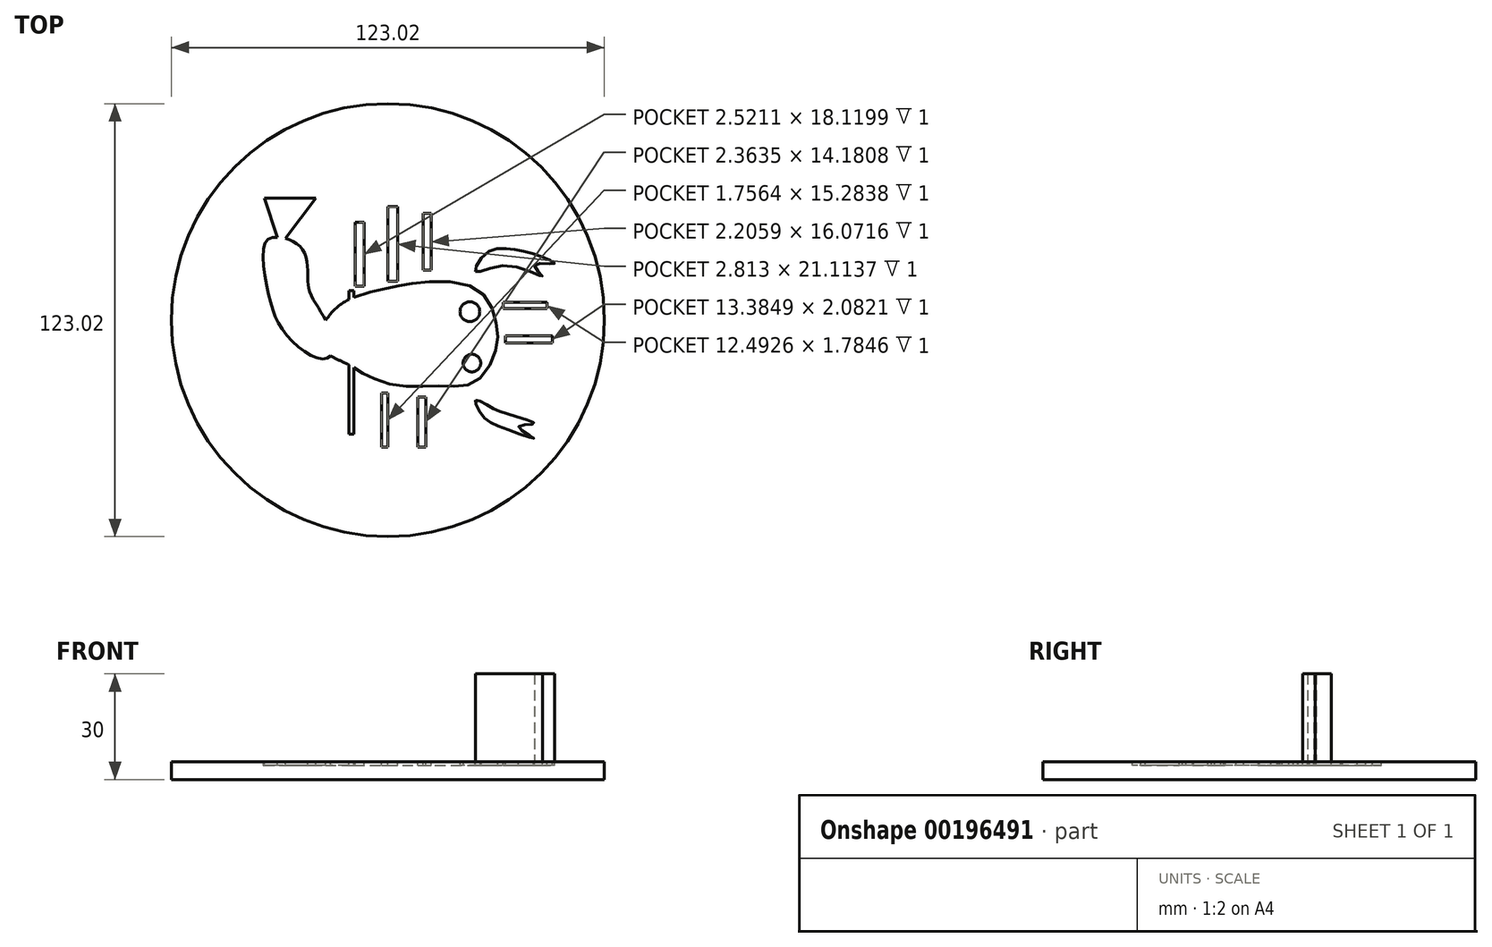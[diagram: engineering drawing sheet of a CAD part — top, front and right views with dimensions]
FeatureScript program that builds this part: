
annotation { "Feature Type Name" : "Feature", "Feature Type Description" : "" }
export const myFeature = defineFeature(function(context is Context, id is Id, definition is map)
    precondition{}
    {
        {
            var Q0;
            Q0=qCreatedBy(makeId("Top.planeOp"),FACE);
            var sketch = newSketch(context, id + "F0", { "sketchPlane" : qUnion([Q0])});
            skCircle(sketch, "E0", {"center": v(0, 0) * mm, "radius": 61.51 * mm});
            skSolve(sketch);
        }
        {
            var Q0;
            Q0=makeQuery(id+"F0.imprint","IMPRINT",FACE,{"disambiguationData":[TD([[makeQuery(id+"F0.imprint","IMPRINT",EDGE,{"derivedFrom":sQuery(id+"F0.wireOp",EDGE,"E0")}),1.0]])]});
            extrude(context, id + "F1", {"entities" : qUnion([Q0]), "depth" : 5 * mm});
        }
        {
            var Q0;
            Q0=makeQuery(id+"F1.opExtrude","CAP_FACE",FACE,{"disambiguationData":[OSD([sQuery(id+"F0.wireOp",EDGE,"E0")])],"isStart":false});
            var sketch = newSketch(context, id + "F2", { "sketchPlane" : qUnion([Q0])});
            skFitSpline(sketch, "E1", {"points": [v(-20.5, -6.6) * mm, v(-17.69, 0) * mm, v(-11.8, 5.47) * mm, v(0, 9.12) * mm, v(7.86, 10.53) * mm, v(24.7, 9.12) * mm, v(30.6, 0) * mm, v(30.6, -8.84) * mm, v(24.43, -17.83) * mm, v(15.44, -18.67) * mm, v(3.37, -18.67) * mm, v(-6.74, -15.3) * mm, v(-11.51, -12.5) * mm, v(-20.5, -6.6) * mm]});
            skSolve(sketch);
        }
        {
            var Q0;
            Q0=makeQuery(id+"F2.imprint","IMPRINT",FACE,{"disambiguationData":[TD([[makeQuery(id+"F2.imprint","IMPRINT",EDGE,{"derivedFrom":sQuery(id+"F2.wireOp",EDGE,"E1")}),-1.0]])]});
            extrude(context, id + "F3", {"entities" : qUnion([Q0]), "operationType" : NewBodyOperationType.REMOVE, "oppositeDirection" : true, "depth" : 1 * mm});
        }
        {
            var Q0;
            Q0=makeQuery(id+"F1.opExtrude","CAP_FACE",FACE,{"disambiguationData":[OSD([sQuery(id+"F0.wireOp",EDGE,"E0")])],"isStart":false});
            var sketch = newSketch(context, id + "F4", { "sketchPlane" : qUnion([Q0])});
            skFitSpline(sketch, "E2", {"points": [v(-30.6, 23.44) * mm, v(-34.81, 22.04) * mm, v(-33.97, 7.72) * mm, v(-29.76, -2.95) * mm, v(-20.78, -10.53) * mm, v(-16.28, -10.18) * mm, v(-16, -5.47) * mm, v(-17.69, 0) * mm, v(-22.18, 8) * mm, v(-22.74, 13.05) * mm, v(-24.43, 20.35) * mm, v(-30.6, 23.44) * mm]});
            skSolve(sketch);
        }
        {
            var Q0;
            {var subQ0=sQuery(id+"F4.wireOp",EDGE,"E2");var subQ1=makeQuery(id+"F3.boolean.opBoolean","COPY",EDGE,{"derivedFrom":makeQuery(id+"F3.opExtrude","CAP_EDGE",EDGE,{"disambiguationData":[OSD([sQuery(id+"F2.wireOp",EDGE,"E1")])],"isStart":true})});var subQ2=makeQuery(id+"F4.imprint","INTERSECT",VERTEX,{"disambiguationData":[OD(0.0)],"derivedFrom":[subQ1,subQ0]});Q0=makeQuery(id+"F4.imprint","IMPRINT",FACE,{"disambiguationData":[TD([[makeQuery(id+"F4.imprint","IMPRINT",EDGE,{"disambiguationData":[TD([[subQ2,-1.0]])],"derivedFrom":subQ0}),1.0]])]});}
            var Q1;
            {var subQ0=sQuery(id+"F4.wireOp",EDGE,"E2");var subQ1=makeQuery(id+"F3.boolean.opBoolean","COPY",EDGE,{"derivedFrom":makeQuery(id+"F3.opExtrude","CAP_EDGE",EDGE,{"disambiguationData":[OSD([sQuery(id+"F2.wireOp",EDGE,"E1")])],"isStart":true})});var subQ2=makeQuery(id+"F4.imprint","INTERSECT",VERTEX,{"disambiguationData":[OD(0.0)],"derivedFrom":[subQ1,subQ0]});Q1=makeQuery(id+"F4.imprint","IMPRINT",FACE,{"disambiguationData":[TD([[makeQuery(id+"F4.imprint","IMPRINT",EDGE,{"disambiguationData":[TD([[subQ2,1.0]])],"derivedFrom":subQ0}),1.0]])]});}
            extrude(context, id + "F5", {"entities" : qUnion([Q0, Q1]), "operationType" : NewBodyOperationType.REMOVE, "oppositeDirection" : true, "depth" : 1 * mm});
        }
        {
            var Q0;
            Q0=makeQuery(id+"F1.opExtrude","CAP_FACE",FACE,{"disambiguationData":[OSD([sQuery(id+"F0.wireOp",EDGE,"E0")])],"isStart":false});
            var sketch = newSketch(context, id + "F6", { "sketchPlane" : qUnion([Q0])});
            skLineSegment(sketch, "E3", {"start": v(-35.1, 34.67) * mm, "end": v(-30.6, 21.2) * mm});
            skLineSegment(sketch, "E4", {"start": v(-30.6, 21.2) * mm, "end": v(-20.5, 34.67) * mm});
            skLineSegment(sketch, "E5", {"start": v(-20.5, 34.67) * mm, "end": v(-35.1, 34.67) * mm});
            skSolve(sketch);
        }
        {
            var Q0;
            {var subQ0=sQuery(id+"F6.wireOp",EDGE,"E4");var subQ1=sQuery(id+"F6.wireOp",EDGE,"E3");var subQ2=makeQuery(id+"F6.imprint","INTERSECT",VERTEX,{"derivedFrom":[subQ1,subQ0]});Q0=makeQuery(id+"F6.imprint","IMPRINT",FACE,{"disambiguationData":[TD([[makeQuery(id+"F6.imprint","IMPRINT",EDGE,{"disambiguationData":[TD([[subQ2,1.0]])],"derivedFrom":subQ1}),1.0]])]});}
            var Q1;
            {var subQ0=sQuery(id+"F6.wireOp",EDGE,"E5");Q1=makeQuery(id+"F6.imprint","IMPRINT",FACE,{"disambiguationData":[TD([[makeQuery(id+"F6.imprint","IMPRINT",EDGE,{"derivedFrom":subQ0}),1.0]])]});}
            extrude(context, id + "F7", {"entities" : qUnion([Q0, Q1]), "operationType" : NewBodyOperationType.REMOVE, "oppositeDirection" : true, "depth" : 1 * mm});
        }
        {
            var Q0;
            Q0=makeQuery(id+"F7.boolean.opBoolean","MERGE",FACE,{"derivedFrom":[makeQuery(id+"F5.boolean.opBoolean","MERGE",FACE,{"derivedFrom":[makeQuery(id+"F3.boolean.opBoolean","COPY",FACE,{"derivedFrom":makeQuery(id+"F3.opExtrude","CAP_FACE",FACE,{"disambiguationData":[OSD([sQuery(id+"F2.wireOp",EDGE,"E1")])],"isStart":false})}),makeQuery(id+"F5.opExtrude","CAP_FACE",FACE,{"disambiguationData":[OSD([sQuery(id+"F4.wireOp",EDGE,"E2")])],"isStart":false})]}),makeQuery(id+"F7.opExtrude","CAP_FACE",FACE,{"disambiguationData":[OSD([sQuery(id+"F6.wireOp",EDGE,"E3"),sQuery(id+"F6.wireOp",EDGE,"E4"),sQuery(id+"F6.wireOp",EDGE,"E5")])],"isStart":false})]});
            var sketch = newSketch(context, id + "F8", { "sketchPlane" : qUnion([Q0])});
            skCircle(sketch, "E6", {"center": v(23.3, 2.39) * mm, "radius": 2.8 * mm});
            skCircle(sketch, "E7", {"center": v(23.86, -12.21) * mm, "radius": 2.51 * mm});
            skSolve(sketch);
        }
        {
            var Q0;
            Q0=makeQuery(id+"F8.imprint","IMPRINT",FACE,{"disambiguationData":[TD([[makeQuery(id+"F8.imprint","IMPRINT",EDGE,{"derivedFrom":sQuery(id+"F8.wireOp",EDGE,"E6")}),1.0]])]});
            var Q1;
            Q1=makeQuery(id+"F8.imprint","IMPRINT",FACE,{"disambiguationData":[TD([[makeQuery(id+"F8.imprint","IMPRINT",EDGE,{"derivedFrom":sQuery(id+"F8.wireOp",EDGE,"E7")}),1.0]])]});
            extrude(context, id + "F9", {"entities" : qUnion([Q0, Q1]), "operationType" : NewBodyOperationType.ADD, "depth" : 1 * mm});
        }
        {
            var Q0;
            Q0=makeQuery(id+"F1.opExtrude","CAP_FACE",FACE,{"disambiguationData":[OSD([sQuery(id+"F0.wireOp",EDGE,"E0")])],"isStart":false});
            var sketch = newSketch(context, id + "F10", { "sketchPlane" : qUnion([Q0])});
            skLineSegment(sketch, "E8.bottom", {"start": v(-9.32, 9.65) * mm, "end": v(-6.8, 9.65) * mm});
            skLineSegment(sketch, "E8.top", {"start": v(-9.32, 27.77) * mm, "end": v(-6.8, 27.77) * mm});
            skLineSegment(sketch, "E8.left", {"start": v(-9.32, 9.65) * mm, "end": v(-9.32, 27.77) * mm});
            skLineSegment(sketch, "E8.right", {"start": v(-6.8, 9.65) * mm, "end": v(-6.8, 27.77) * mm});
            skLineSegment(sketch, "E9.bottom", {"start": v(0, 11.07) * mm, "end": v(2.81, 11.07) * mm});
            skLineSegment(sketch, "E9.top", {"start": v(0, 32.18) * mm, "end": v(2.81, 32.18) * mm});
            skLineSegment(sketch, "E9.left", {"start": v(0, 11.07) * mm, "end": v(0, 32.18) * mm});
            skLineSegment(sketch, "E9.right", {"start": v(2.81, 11.07) * mm, "end": v(2.81, 32.18) * mm});
            skLineSegment(sketch, "E10.bottom", {"start": v(10.06, 14.22) * mm, "end": v(12.27, 14.22) * mm});
            skLineSegment(sketch, "E10.top", {"start": v(10.06, 30.29) * mm, "end": v(12.27, 30.29) * mm});
            skLineSegment(sketch, "E10.left", {"start": v(10.06, 14.22) * mm, "end": v(10.06, 30.29) * mm});
            skLineSegment(sketch, "E10.right", {"start": v(12.27, 14.22) * mm, "end": v(12.27, 30.29) * mm});
            skLineSegment(sketch, "E11.bottom", {"start": v(-11.05, -16.66) * mm, "end": v(-9.63, -16.66) * mm});
            skLineSegment(sketch, "E11.top", {"start": v(-11.05, -32.42) * mm, "end": v(-9.63, -32.42) * mm});
            skLineSegment(sketch, "E11.left", {"start": v(-11.05, -16.66) * mm, "end": v(-11.05, -32.42) * mm});
            skLineSegment(sketch, "E11.right", {"start": v(-9.63, -16.66) * mm, "end": v(-9.63, -32.42) * mm});
            skLineSegment(sketch, "E12.bottom", {"start": v(-1.76, -20.76) * mm, "end": v(0, -20.76) * mm});
            skLineSegment(sketch, "E12.top", {"start": v(-1.76, -36.05) * mm, "end": v(0, -36.05) * mm});
            skLineSegment(sketch, "E12.left", {"start": v(-1.76, -20.76) * mm, "end": v(-1.76, -36.05) * mm});
            skLineSegment(sketch, "E12.right", {"start": v(0, -20.76) * mm, "end": v(0, -36.05) * mm});
            skLineSegment(sketch, "E13.bottom", {"start": v(8.49, -21.86) * mm, "end": v(10.85, -21.86) * mm});
            skLineSegment(sketch, "E13.top", {"start": v(8.49, -36.05) * mm, "end": v(10.85, -36.05) * mm});
            skLineSegment(sketch, "E13.left", {"start": v(8.49, -21.86) * mm, "end": v(8.49, -36.05) * mm});
            skLineSegment(sketch, "E13.right", {"start": v(10.85, -21.86) * mm, "end": v(10.85, -36.05) * mm});
            skLineSegment(sketch, "E14", {"start": v(24.71, 11.85) * mm, "end": v(38.42, 23.36) * mm});
            skLineSegment(sketch, "E15", {"start": v(38.42, 23.36) * mm, "end": v(40.21, 21.22) * mm});
            skLineSegment(sketch, "E16", {"start": v(40.31, 21.3) * mm, "end": v(26.6, 9.5) * mm});
            skLineSegment(sketch, "E17", {"start": v(26.6, 9.5) * mm, "end": v(24.71, 11.85) * mm});
            skLineSegment(sketch, "E18", {"start": v(29.91, -16.82) * mm, "end": v(26.92, -19.82) * mm});
            skLineSegment(sketch, "E19", {"start": v(26.92, -19.82) * mm, "end": v(38.42, -31.32) * mm});
            skLineSegment(sketch, "E20", {"start": v(38.42, -31.16) * mm, "end": v(41.42, -27.54) * mm});
            skLineSegment(sketch, "E21", {"start": v(41.42, -27.54) * mm, "end": v(29.91, -16.82) * mm});
            skSolve(sketch);
        }
        {
            var Q0;
            Q0=makeQuery(id+"F10.imprint","IMPRINT",FACE,{"disambiguationData":[TD([[makeQuery(id+"F10.imprint","IMPRINT",EDGE,{"derivedFrom":sQuery(id+"F10.wireOp",EDGE,"E8.bottom")}),1.0]])]});
            var Q1;
            Q1=makeQuery(id+"F10.imprint","IMPRINT",FACE,{"disambiguationData":[TD([[makeQuery(id+"F10.imprint","IMPRINT",EDGE,{"derivedFrom":sQuery(id+"F10.wireOp",EDGE,"E9.bottom")}),1.0]])]});
            var Q2;
            Q2=makeQuery(id+"F10.imprint","IMPRINT",FACE,{"disambiguationData":[TD([[makeQuery(id+"F10.imprint","IMPRINT",EDGE,{"derivedFrom":sQuery(id+"F10.wireOp",EDGE,"E10.bottom")}),1.0]])]});
            var Q3;
            Q3=makeQuery(id+"F10.imprint","IMPRINT",FACE,{"disambiguationData":[TD([[makeQuery(id+"F10.imprint","IMPRINT",EDGE,{"derivedFrom":sQuery(id+"F10.wireOp",EDGE,"E11.bottom")}),-1.0]])]});
            var Q4;
            Q4=makeQuery(id+"F10.imprint","IMPRINT",FACE,{"disambiguationData":[TD([[makeQuery(id+"F10.imprint","IMPRINT",EDGE,{"derivedFrom":sQuery(id+"F10.wireOp",EDGE,"E12.bottom")}),-1.0]])]});
            var Q5;
            Q5=makeQuery(id+"F10.imprint","IMPRINT",FACE,{"disambiguationData":[TD([[makeQuery(id+"F10.imprint","IMPRINT",EDGE,{"derivedFrom":sQuery(id+"F10.wireOp",EDGE,"E13.bottom")}),-1.0]])]});
            extrude(context, id + "F11", {"entities" : qUnion([Q0, Q1, Q2, Q3, Q4, Q5]), "operationType" : NewBodyOperationType.REMOVE, "oppositeDirection" : true, "depth" : 1 * mm});
        }
        {
            var Q0;
            Q0=makeQuery(id+"F1.opExtrude","CAP_FACE",FACE,{"disambiguationData":[OSD([sQuery(id+"F0.wireOp",EDGE,"E0")])],"isStart":false});
            var sketch = newSketch(context, id + "F12", { "sketchPlane" : qUnion([Q0])});
            skFitSpline(sketch, "E22", {"points": [v(24.93, 13.88) * mm, v(28.12, 19.19) * mm, v(35.72, 20.07) * mm, v(43.86, 17.95) * mm, v(47.22, 16) * mm, v(41.74, 15.65) * mm, v(43.86, 12.47) * mm, v(34.3, 15.47) * mm, v(24.93, 13.88) * mm]});
            skFitSpline(sketch, "E23", {"points": [v(24.93, -22.73) * mm, v(26.7, -26.97) * mm, v(33.78, -31.04) * mm, v(41.38, -33.52) * mm, v(37.14, -30.33) * mm, v(41.56, -29.45) * mm, v(35.01, -26.97) * mm, v(29, -24.68) * mm, v(24.93, -22.73) * mm]});
            skSolve(sketch);
        }
        {
            var Q0;
            Q0=makeQuery(id+"F12.imprint","IMPRINT",FACE,{"disambiguationData":[TD([[makeQuery(id+"F12.imprint","IMPRINT",EDGE,{"derivedFrom":sQuery(id+"F12.wireOp",EDGE,"E22")}),-1.0]])]});
            var Q1;
            Q1=makeQuery(id+"F12.imprint","IMPRINT",FACE,{"disambiguationData":[TD([[makeQuery(id+"F12.imprint","IMPRINT",EDGE,{"derivedFrom":sQuery(id+"F12.wireOp",EDGE,"E23")}),1.0]])]});
            extrude(context, id + "F13", {"entities" : qUnion([Q0, Q1]), "operationType" : NewBodyOperationType.REMOVE, "oppositeDirection" : true, "depth" : 1 * mm});
        }
        {
            var Q0;
            Q0=makeQuery(id+"F1.opExtrude","CAP_FACE",FACE,{"disambiguationData":[OSD([sQuery(id+"F0.wireOp",EDGE,"E0")])],"isStart":false});
            var sketch = newSketch(context, id + "F14", { "sketchPlane" : qUnion([Q0])});
            skLineSegment(sketch, "E24.bottom", {"start": v(32.75, 5.06) * mm, "end": v(45.25, 5.06) * mm});
            skLineSegment(sketch, "E24.top", {"start": v(32.75, 3.28) * mm, "end": v(45.25, 3.28) * mm});
            skLineSegment(sketch, "E24.left", {"start": v(32.75, 5.06) * mm, "end": v(32.75, 3.28) * mm});
            skLineSegment(sketch, "E24.right", {"start": v(45.25, 5.06) * mm, "end": v(45.25, 3.28) * mm});
            skLineSegment(sketch, "E25.bottom", {"start": v(33.35, -4.46) * mm, "end": v(46.73, -4.46) * mm});
            skLineSegment(sketch, "E25.top", {"start": v(33.35, -6.54) * mm, "end": v(46.73, -6.54) * mm});
            skLineSegment(sketch, "E25.left", {"start": v(33.35, -4.46) * mm, "end": v(33.35, -6.54) * mm});
            skLineSegment(sketch, "E25.right", {"start": v(46.73, -4.46) * mm, "end": v(46.73, -6.54) * mm});
            skSolve(sketch);
        }
        {
            var Q0;
            Q0=makeQuery(id+"F14.imprint","IMPRINT",FACE,{"disambiguationData":[TD([[makeQuery(id+"F14.imprint","IMPRINT",EDGE,{"derivedFrom":sQuery(id+"F14.wireOp",EDGE,"E24.bottom")}),-1.0]])]});
            var Q1;
            Q1=makeQuery(id+"F14.imprint","IMPRINT",FACE,{"disambiguationData":[TD([[makeQuery(id+"F14.imprint","IMPRINT",EDGE,{"derivedFrom":sQuery(id+"F14.wireOp",EDGE,"E25.bottom")}),-1.0]])]});
            extrude(context, id + "F15", {"entities" : qUnion([Q0, Q1]), "operationType" : NewBodyOperationType.REMOVE, "oppositeDirection" : true, "depth" : 1 * mm});
        }
        {
            var Q0;
            Q0=makeQuery(id+"F12.imprint","IMPRINT",FACE,{"disambiguationData":[TD([[makeQuery(id+"F12.imprint","IMPRINT",EDGE,{"derivedFrom":sQuery(id+"F12.wireOp",EDGE,"E22")}),-1.0]])]});
            extrude(context, id + "F16", {"entities" : qUnion([Q0]), "operationType" : NewBodyOperationType.ADD, "depth" : 25 * mm});
        }
        {
            var Q0;
            Q0=makeQuery(id+"F11.boolean.opBoolean","COPY",FACE,{"derivedFrom":makeQuery(id+"F11.opExtrude","SWEPT_FACE",FACE,{"disambiguationData":[OSD([sQuery(id+"F10.wireOp",EDGE,"E11.bottom")])]})});
            extrude(context, id + "F17", {"entities" : qUnion([Q0]), "operationType" : NewBodyOperationType.REMOVE, "oppositeDirection" : true, "depth" : 25 * mm});
        }
    });
